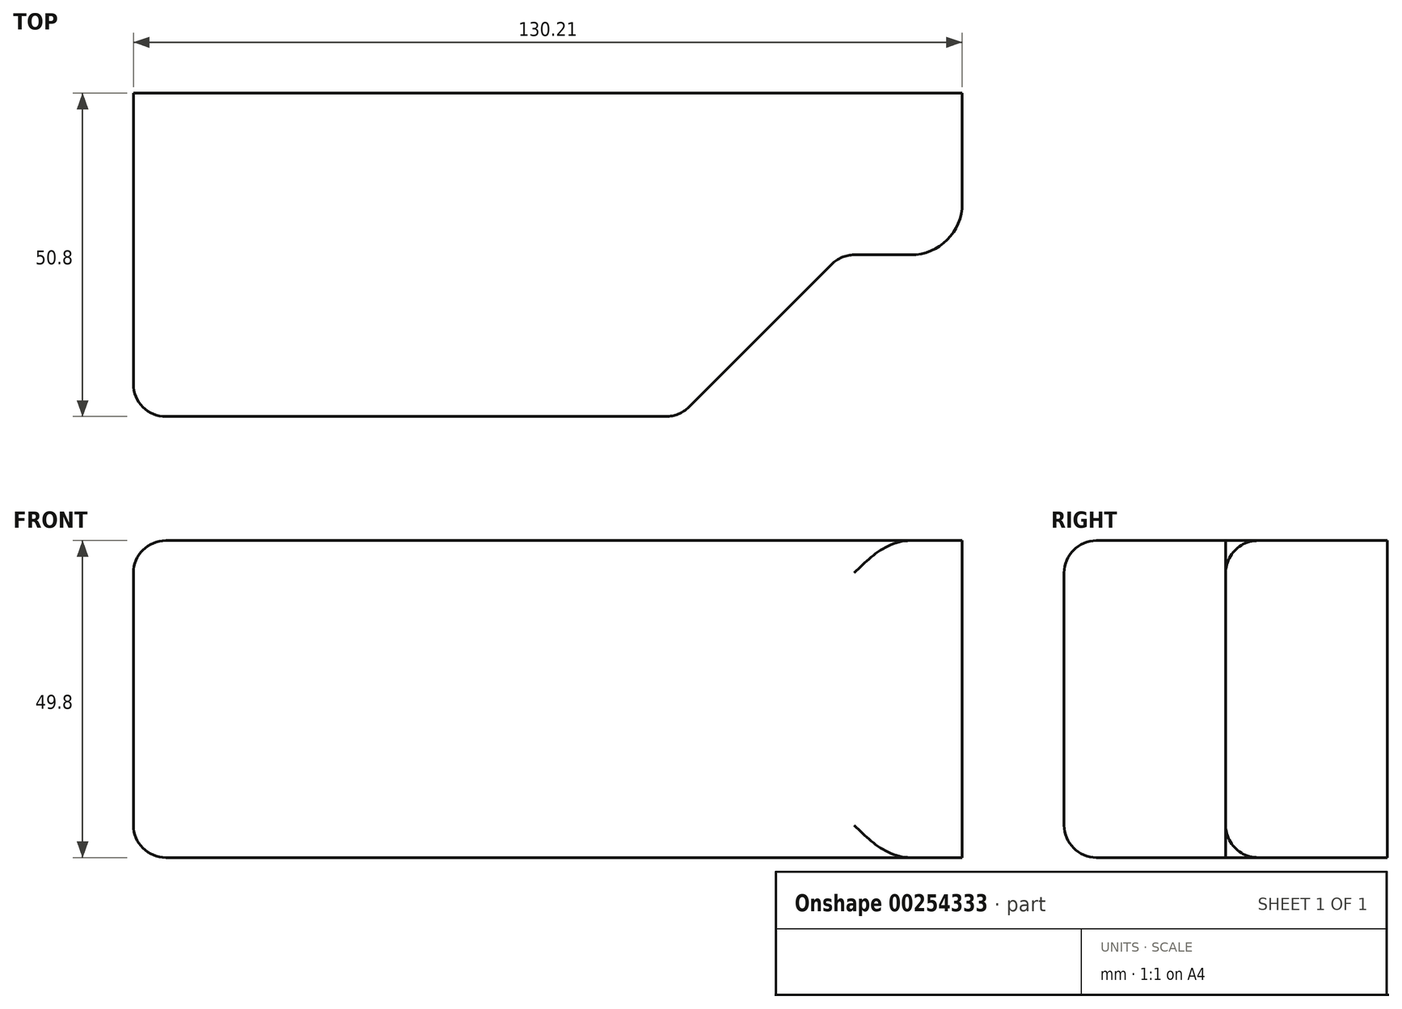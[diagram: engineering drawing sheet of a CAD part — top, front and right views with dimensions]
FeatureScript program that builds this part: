
annotation { "Feature Type Name" : "Feature", "Feature Type Description" : "" }
export const myFeature = defineFeature(function(context is Context, id is Id, definition is map)
    precondition{}
    {
        {
            var Q0;
            Q0=qCreatedBy(makeId("Front.planeOp"),FACE);
            var sketch = newSketch(context, id + "F0", { "sketchPlane" : qUnion([Q0])});
            skLineSegment(sketch, "E0.bottom", {"start": v(-55.58, 24.9) * mm, "end": v(55.58, 24.9) * mm});
            skLineSegment(sketch, "E0.top", {"start": v(-55.58, -24.9) * mm, "end": v(55.58, -24.9) * mm});
            skLineSegment(sketch, "E0.left", {"start": v(-55.58, 24.9) * mm, "end": v(-55.58, -24.9) * mm});
            skLineSegment(sketch, "E0.right", {"start": v(55.58, 24.9) * mm, "end": v(55.58, -24.9) * mm});
            skPoint(sketch, "E0.middle", {"position": v(0, 0) * mm});
            skSolve(sketch);
        }
        {
            var Q0;
            Q0=makeQuery(id+"F0.imprint","IMPRINT",FACE,{"disambiguationData":[TD([[makeQuery(id+"F0.imprint","IMPRINT",EDGE,{"derivedFrom":sQuery(id+"F0.wireOp",EDGE,"E0.bottom")}),-1.0]])]});
            extrude(context, id + "F1", {"entities" : qUnion([Q0]), "depth" : 50.8 * mm});
        }
        {
            var Q0;
            Q0=makeQuery(id+"F1.opExtrude","CAP_EDGE",EDGE,{"disambiguationData":[OSD([sQuery(id+"F0.wireOp",EDGE,"E0.left")])],"isStart":false});
            fillet(context, id + "F2", {"entities" : qUnion([Q0]), "radius" : 5.08 * mm, "tangentPropagation" : true, "allowEdgeOverflow" : false});
        }
        {
            var Q0;
            Q0=makeQuery(id+"F1.opExtrude","CAP_EDGE",EDGE,{"disambiguationData":[OSD([sQuery(id+"F0.wireOp",EDGE,"E0.right")])],"isStart":false});
            chamfer(context, id + "F3", {"entities" : qUnion([Q0]), "width" : 25.4 * mm, "tangentPropagation" : true});
        }
        {
            var Q0;
            Q0=makeQuery(id+"F1.opExtrude","SWEPT_FACE",FACE,{"disambiguationData":[OSD([sQuery(id+"F0.wireOp",EDGE,"E0.right")])]});
            var sketch = newSketch(context, id + "F4", { "sketchPlane" : qUnion([Q0])});
            skLineSegment(sketch, "E1.bottom", {"start": v(0, -24.9) * mm, "end": v(-25.4, -24.9) * mm});
            skLineSegment(sketch, "E1.top", {"start": v(0, 24.9) * mm, "end": v(-25.4, 24.9) * mm});
            skLineSegment(sketch, "E1.left", {"start": v(0, -24.9) * mm, "end": v(0, 24.9) * mm});
            skLineSegment(sketch, "E1.right", {"start": v(-25.4, -24.9) * mm, "end": v(-25.4, 24.9) * mm});
            skSolve(sketch);
        }
        {
            var Q0;
            Q0 = qSketchRegion(id + "F4", true);
            extrude(context, id + "F5", {"entities" : qUnion([Q0]), "operationType" : NewBodyOperationType.ADD, "depth" : 19.05 * mm});
        }
        {
            var Q0;
            Q0=makeQuery(id+"F5.opExtrude","CAP_EDGE",EDGE,{"disambiguationData":[OSD([sQuery(id+"F4.wireOp",EDGE,"E1.right")])],"isStart":false});
            fillet(context, id + "F6", {"entities" : qUnion([Q0]), "radius" : 8.06 * mm, "tangentPropagation" : true, "allowEdgeOverflow" : false});
        }
        {
            var Q0;
            {var subQ0=sQuery(id+"F0.wireOp",EDGE,"E0.right");Q0=makeQuery(id+"F3.opChamfer","BLEND_EDGE",EDGE,{"blendedFrom":[makeQuery(id+"F1.opExtrude","CAP_EDGE",EDGE,{"disambiguationData":[OSD([subQ0])],"isStart":false}),makeQuery(id+"F1.opExtrude","CAP_FACE",FACE,{"disambiguationData":[OSD([sQuery(id+"F0.wireOp",EDGE,"E0.bottom"),sQuery(id+"F0.wireOp",EDGE,"E0.top"),sQuery(id+"F0.wireOp",EDGE,"E0.left"),subQ0])],"isStart":false})],"blendedInto":[makeQuery(id+"F1.opExtrude","CAP_FACE",FACE,{"disambiguationData":[OSD([sQuery(id+"F0.wireOp",EDGE,"E0.bottom"),sQuery(id+"F0.wireOp",EDGE,"E0.top"),sQuery(id+"F0.wireOp",EDGE,"E0.left"),subQ0])],"isStart":false})]});}
            var Q1;
            Q1=makeQuery(id+"F3.opChamfer","BLEND_FACE",FACE,{"disambiguationData":[OSD([sQuery(id+"F0.wireOp",EDGE,"E0.right")])]});
            fillet(context, id + "F7", {"entities" : qUnion([Q0, Q1]), "radius" : 5.08 * mm, "tangentPropagation" : true, "allowEdgeOverflow" : false});
        }
        {
            var Q0;
            Q0=makeQuery(id+"F1.opExtrude","CAP_EDGE",EDGE,{"disambiguationData":[OSD([sQuery(id+"F0.wireOp",EDGE,"E0.top")])],"isStart":false});
            var Q1;
            Q1=makeQuery(id+"F1.opExtrude","CAP_EDGE",EDGE,{"disambiguationData":[OSD([sQuery(id+"F0.wireOp",EDGE,"E0.bottom")])],"isStart":false});
            fillet(context, id + "F8", {"entities" : qUnion([Q0, Q1]), "radius" : 5.08 * mm, "tangentPropagation" : true, "allowEdgeOverflow" : false});
        }
    });
